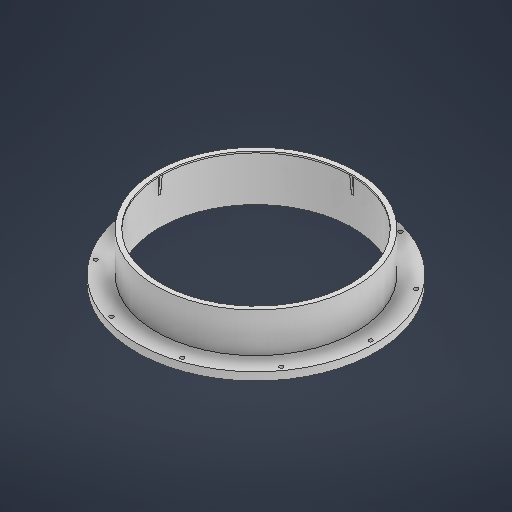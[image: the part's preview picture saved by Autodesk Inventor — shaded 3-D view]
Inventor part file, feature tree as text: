
AUTODESK INVENTOR PART (.ipt)
format: ipt  version: 2025 (Build 290162000, 162)  size: 520,192 bytes
history: native  units: in
note: dims shown in document units (in); Inventor stores cm internally (conversion verified against a paired STEP export)
features: rib x44, sketch x28, other x12, extrude x5, plane x1
ambient origin geometry x8: Origin, YZ Plane, XZ Plane, XY Plane, X Axis, Y Axis, Z Axis, Center Point
bodies: Solid1 (feature_tree)
feature tree (90):
  other  "Table"
  other  "C .Replace - 01"
  other  "C .Replace - 02"
  other  "C .Replace - 03"
  other  "C .Replace - 04"
  other  "C .Replace - 05"
  other  "C .Replace - 06"
  other  "C .Replace - 07"
  other  "C .Replace - 08"
  other  "C .Replace - 09"
  other  "C .Replace - 10"
  other  "C .Replace - Face"
  sketch  "Sketch1"  dims[d5=0.0in d7=0.0in]
  extrude  "Extrusion1"  TaperAngle=0.0deg  [1 undecoded]
  extrude  "Extrusion2"  Depth=11.4173in
  sketch  "Sketch2"  dims[d28=0.1969in d29=3.937in d31=360.0deg]
  extrude  "Extrusion7"  Depth=3.937in TaperAngle=360.0deg
  plane  "Work Plane2"
  extrude  "Extrusion8"  Depth=0.3937in
  extrude  "Extrusion30"  Depth=0.2165in
  sketch  "Sketch26"  dims[d236=0.3937in d237=0.0in]
  rib  "Rib2"
  rib  "Rib3"
  sketch  "Sketch27"  dims[d239=0.8661in]
  rib  "Rib4"
  rib  "Rib5"
  sketch  "Sketch28"  dims[d240=0.8661in]
  rib  "Rib6"
  rib  "Rib7"
  sketch  "Sketch29"  dims[d247=0.0984in]
  rib  "Rib8"
  rib  "Rib9"
  sketch  "Sketch30"  dims[d248=0.1181in d249=0.0in d250=0.0in d251=0.0394in d252=0.0394in]
  rib  "Rib10"
  rib  "Rib11"
  sketch  "Sketch31"  dims[d253=0.0984in]
  rib  "Rib12"
  rib  "Rib13"
  sketch  "Sketch32"  dims[d254=0.1181in d255=0.0in d256=0.0in d257=0.0394in d258=0.0394in]
  rib  "Rib14"
  rib  "Rib15"
  sketch  "Sketch33"  dims[d259=0.8661in]
  rib  "Rib16"
  rib  "Rib17"
  sketch  "Sketch34"  dims[d260=0.8661in]
  rib  "Rib18"
  rib  "Rib19"
  sketch  "Sketch35"  dims[d261=0.0984in]
  rib  "Rib20"
  rib  "Rib21"
  sketch  "Sketch36"  dims[d262=0.1181in d263=0.0in d264=0.0in d265=0.0394in d266=0.0394in]
  rib  "Rib22"
  rib  "Rib23"
  sketch  "Sketch37"  dims[d267=0.0984in]
  rib  "Rib24"
  rib  "Rib25"
  sketch  "Sketch38"  dims[d268=0.1181in d269=0.0in d270=0.0in d271=0.0394in d272=0.0394in]
  rib  "Rib26"
  rib  "Rib27"
  sketch  "Sketch39"  dims[d274=0.8661in]
  rib  "Rib28"
  rib  "Rib29"
  sketch  "Sketch40"  dims[d275=0.8661in]
  rib  "Rib30"
  rib  "Rib31"
  sketch  "Sketch41"  dims[d276=0.0984in]
  rib  "Rib32"
  rib  "Rib33"
  sketch  "Sketch42"  dims[d277=0.1181in d278=0.0in d279=0.0in d280=0.0394in d281=0.0394in]
  rib  "Rib34"
  rib  "Rib35"
  sketch  "Sketch43"  dims[d282=0.0984in]
  rib  "Rib36"
  rib  "Rib37"
  sketch  "Sketch44"  dims[d283=0.1181in d284=0.0in d285=0.0in d286=0.0394in d287=0.0394in]
  rib  "Rib38"
  rib  "Rib39"
  sketch  "Sketch45"  dims[d288=0.8661in]
  rib  "Rib40"
  rib  "Rib41"
  sketch  "Sketch46"  dims[d289=0.8661in]
  rib  "Rib42"
  rib  "Rib43"
  sketch  "Sketch47"  dims[d290=0.0984in d291=0.1181in d292=0.0in d293=0.0in d294=0.0394in d295=0.0394in d296=0.0984in d297=0.1181in d298=0.0in d299=0.0in d300=0.0394in d301=0.0394in d302=0.8661in d303=0.8661in d304=0.0984in d305=0.1181in d306=0.0in d307=0.0in d308=0.0394in d309=0.0394in d310=0.0984in d311=0.1181in d312=0.0in d313=0.0in d314=0.0394in d315=0.0394in d316=0.8661in d317=0.8661in d318=0.0984in d319=0.1181in d320=0.0in d321=0.0in d322=0.0394in d323=0.0394in d324=0.0984in d325=0.1181in d326=0.0in d327=0.0in d328=0.0394in d329=0.0394in d330=0.8661in d331=0.8661in d332=0.0984in d333=0.1181in d334=0.0in d335=0.0in d336=0.0394in d337=0.0394in d338=0.0984in d339=0.1181in d340=0.0in d341=0.0in d342=0.0394in d343=0.0394in d344=0.8661in d345=0.8661in d346=0.0984in d347=0.1181in d348=0.0in d349=0.0in d350=0.0394in d351=0.0394in d352=0.0984in d353=0.1181in d354=0.0in d355=0.0in d356=0.0394in d357=0.0394in d358=0.8661in d359=0.8661in d360=0.0984in d361=0.1181in d362=0.0in d363=0.0in d364=0.0394in d365=0.0394in d366=0.0984in d367=0.1181in d368=0.0in d369=0.0in d370=0.0394in d371=0.0394in d372=0.8661in d373=0.8661in d374=0.0984in d375=0.1181in d376=0.0in d377=0.0in d378=0.0394in d379=0.0394in d380=0.0984in d381=0.1181in d382=0.0in d383=0.0in d384=0.0394in d385=0.0394in d386=0.8661in d387=0.8661in d388=0.0984in d389=0.1181in d390=0.0in d391=0.0in d392=0.0394in d393=0.0394in d394=0.0984in d395=0.1181in d396=0.0in d397=0.0in d398=0.0394in d399=0.0394in d401=0.8661in d402=0.0984in d403=0.1181in d404=0.0in d405=0.0in d406=0.0394in d407=0.0394in d408=0.0984in d409=0.1181in d410=0.0in d411=0.0in d412=0.0394in d413=0.0394in d414=0.8661in d415=0.8661in d416=0.0984in d417=0.1181in d418=0.0in d419=0.0in d420=0.0394in d421=0.0394in d422=0.0984in d423=0.1181in d424=0.0in d425=0.0in d426=0.0394in d427=0.0394in d428=0.8661in d429=0.8661in d430=0.0984in d431=0.1181in d432=0.0in d433=0.0in d434=0.0394in d435=0.0394in d436=0.0984in d437=0.1181in d438=0.0in d439=0.0in d440=0.0394in d441=0.0394in d442=0.8661in d443=0.8661in d444=0.0984in d445=0.1181in d446=0.0in d447=0.0in d448=0.0394in d449=0.0394in d450=0.0984in d451=0.1181in d452=0.0in d453=0.0in d454=0.0394in d455=0.0394in d456=0.8661in d457=0.8661in d458=0.0984in d459=0.1181in d460=0.0in d461=0.0in d462=0.0394in d463=0.0394in d464=0.0984in d465=0.1181in d466=0.0in d467=0.0in d468=0.0394in d469=0.0394in d470=0.8661in d471=0.8661in d472=0.0984in d473=0.1181in d474=0.0in d475=0.0in d476=0.0394in d477=0.0394in d478=0.0984in d479=0.1181in d480=0.0in d481=0.0in d482=0.0394in d483=0.0394in d484=0.8661in d485=0.8661in d486=0.0984in d487=0.1181in d488=0.0in d489=0.0in d490=0.0394in d491=0.0394in d492=0.0984in d493=0.1181in d494=0.0in d495=0.0in d496=0.0394in d497=0.0394in d498=0.8661in d499=0.8661in d500=0.1181in d501=0.0984in d502=0.0in d503=0.0in d504=0.0394in d505=0.0394in d506=0.0984in d507=0.1181in d508=0.0in d509=0.0in d510=0.0394in d511=0.0394in d512=0.8661in d513=0.8661in d514=0.0984in d515=0.1181in d516=0.0in d517=0.0in d518=0.0394in d519=0.0394in d520=0.0984in d521=0.1181in d522=0.0in d523=0.0in d524=0.0394in d525=0.0394in d526=0.8661in d527=0.0984in d528=0.1181in d529=0.0in d530=0.0in d531=0.0394in d532=0.0394in d533=0.0984in d534=0.1181in d535=0.0in d536=0.0in d537=0.0394in d538=0.0394in d539=0.8661in d540=0.0984in d541=0.1181in d542=0.0in d543=0.0in d544=0.0394in d545=0.0394in d546=0.0984in d547=0.1181in d548=0.0in d549=0.0in d550=0.0394in d551=0.0394in d113=0.0197in d114=0.0344in d115=0.0197in d116=0.0344in d167=0.0197in d168=0.0344in d169=0.0197in d170=0.0344in d215=0.0197in d216=0.0344in d217=0.0197in d218=0.0344in d219=0.0in d220=0.0in]
  rib  "Rib44"
  rib  "Rib45"
  sketch  "Sketch3"  dims[d33=0.3937in d34=0.0in d52=4.5276in]
  sketch  "Sketch Circular Pattern1"  dims[d18=0.0in d27=11.4173in]
  sketch  "Sketch24"  dims[d232=2.3622in d234=360.0deg]
  sketch  "Sketch Circular Pattern4"  dims[d230=4.0157in d231=0.2165in]
note: 1 required parameter value undecoded (feature->parameter linkage not recoverable at this tier; creation-order binding heuristic only, values carry confidence <= 0.55)
